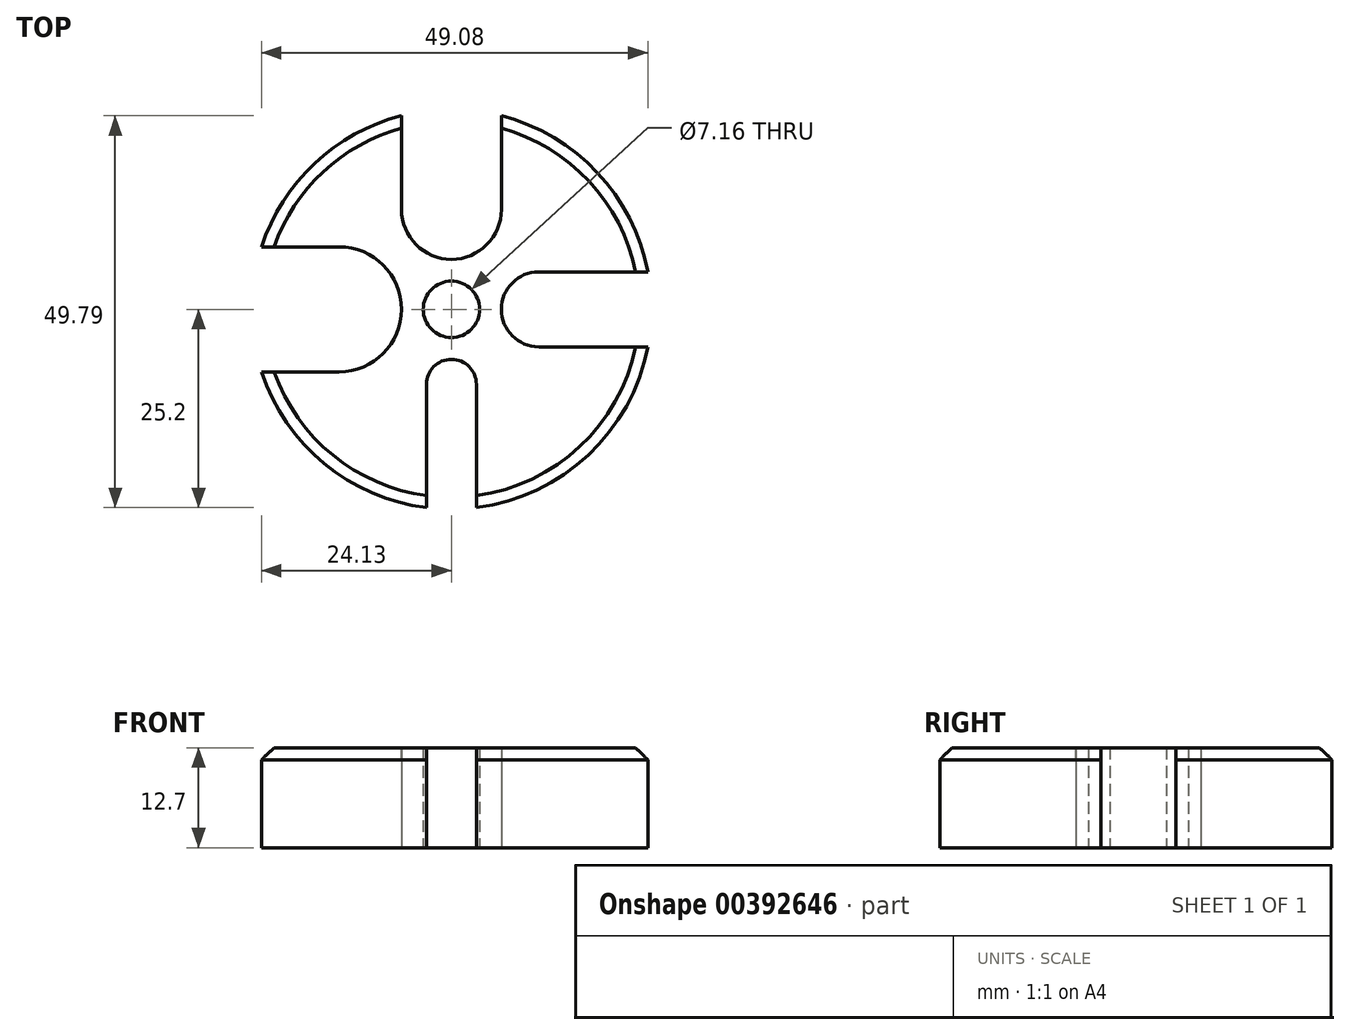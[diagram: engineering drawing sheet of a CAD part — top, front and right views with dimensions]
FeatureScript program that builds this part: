
annotation { "Feature Type Name" : "Feature", "Feature Type Description" : "" }
export const myFeature = defineFeature(function(context is Context, id is Id, definition is map)
    precondition{}
    {
        {
            var Q0;
            Q0=qCreatedBy(makeId("Top.planeOp"),FACE);
            var sketch = newSketch(context, id + "F0", { "sketchPlane" : qUnion([Q0])});
            skArc(sketch, "E0", {"start": v(-24.13, -7.94) * mm, "mid": v(-16.15, -19.6) * mm, "end": v(-3.17, -25.2) * mm});
            skArc(sketch, "E1", {"start": v(-6.35, 12.7) * mm, "mid": v(0, 6.35) * mm, "end": v(6.35, 12.7) * mm});
            skArc(sketch, "E2", {"start": v(11.1, 4.76) * mm, "mid": v(6.34, 0) * mm, "end": v(11.1, -4.76) * mm});
            skArc(sketch, "E3", {"start": v(3.18, -9.53) * mm, "mid": v(0, -6.35) * mm, "end": v(-3.18, -9.53) * mm});
            skArc(sketch, "E4", {"start": v(-14.27, -7.94) * mm, "mid": v(-6.34, 0) * mm, "end": v(-14.27, 7.94) * mm});
            skLineSegment(sketch, "E5", {"start": v(-6.35, 12.7) * mm, "end": v(-6.35, 24.6) * mm});
            skLineSegment(sketch, "E6", {"start": v(6.35, 24.6) * mm, "end": v(6.35, 12.7) * mm});
            skLineSegment(sketch, "E7", {"start": v(11.1, 4.76) * mm, "end": v(24.95, 4.76) * mm});
            skLineSegment(sketch, "E8", {"start": v(11.1, -4.76) * mm, "end": v(24.95, -4.76) * mm});
            skLineSegment(sketch, "E9", {"start": v(-3.18, -9.53) * mm, "end": v(-3.17, -25.2) * mm});
            skLineSegment(sketch, "E10", {"start": v(3.17, -9.53) * mm, "end": v(3.18, -25.2) * mm});
            skLineSegment(sketch, "E11", {"start": v(-14.27, -7.94) * mm, "end": v(-24.13, -7.94) * mm});
            skLineSegment(sketch, "E12", {"start": v(-14.27, 7.94) * mm, "end": v(-24.13, 7.94) * mm});
            skCircle(sketch, "E13", {"center": v(0, 0) * mm, "radius": 3.58 * mm});
            skArc(sketch, "E14.trimOffspring", {"start": v(-6.35, 24.6) * mm, "mid": v(-17.37, 18.54) * mm, "end": v(-24.13, 7.94) * mm});
            skArc(sketch, "E15.trimOffspring", {"start": v(24.95, 4.76) * mm, "mid": v(18.53, 17.38) * mm, "end": v(6.35, 24.6) * mm});
            skArc(sketch, "E16.trimOffspring", {"start": v(3.17, -25.2) * mm, "mid": v(17.38, -18.52) * mm, "end": v(24.95, -4.76) * mm});
            skSolve(sketch);
        }
        {
            var Q0;
            Q0=makeQuery(id+"F0.imprint","IMPRINT",FACE,{"disambiguationData":[TD([[makeQuery(id+"F0.imprint","IMPRINT",EDGE,{"derivedFrom":sQuery(id+"F0.wireOp",EDGE,"E0")}),1.0]])]});
            extrude(context, id + "F1", {"entities" : qUnion([Q0]), "depth" : 12.7 * mm});
        }
        {
            var Q0;
            Q0=makeQuery(id+"F1.opExtrude","CAP_EDGE",EDGE,{"disambiguationData":[OSD([sQuery(id+"F0.wireOp",EDGE,"E14.trimOffspring")])],"isStart":false});
            var Q1;
            Q1=makeQuery(id+"F1.opExtrude","CAP_EDGE",EDGE,{"disambiguationData":[OSD([sQuery(id+"F0.wireOp",EDGE,"E15.trimOffspring")])],"isStart":false});
            var Q2;
            Q2=makeQuery(id+"F1.opExtrude","CAP_EDGE",EDGE,{"disambiguationData":[OSD([sQuery(id+"F0.wireOp",EDGE,"E16.trimOffspring")])],"isStart":false});
            var Q3;
            Q3=makeQuery(id+"F1.opExtrude","CAP_EDGE",EDGE,{"disambiguationData":[OSD([sQuery(id+"F0.wireOp",EDGE,"E0")])],"isStart":false});
            chamfer(context, id + "F2", {"entities" : qUnion([Q0, Q1, Q2, Q3]), "chamferType" : ChamferType.OFFSET_ANGLE, "width" : 1.52 * mm, "oppositeDirection" : false, "angle" : 45 * degree, "tangentPropagation" : true});
        }
    });
